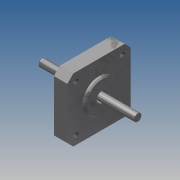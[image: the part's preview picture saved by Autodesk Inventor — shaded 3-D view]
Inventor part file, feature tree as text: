
AUTODESK INVENTOR PART (.ipt)
format: ipt  version: 2015 (Build 190159000, 159)  size: 141,824 bytes
history: native  units: mm
features: sketch x4, extrude x3, chamfer x3, hole x1, projected_geometry x1
ambient origin geometry x8: Origin, YZ Plane, XZ Plane, XY Plane, X Axis, Y Axis, Z Axis, Center Point
bodies: Body1 (feature_tree)
feature tree (12):
  extrude  "Extrusion2"  Depth=42.3mm
  hole  "Bohrung1"  [1 undecoded]
  extrude  "Extrusion3"  Depth=4.0mm
  chamfer  "Fase1"  Distance=4.0mm
  extrude  "Extrusion4"  Depth=2.0mm
  chamfer  "Fase2"  Distance=4.0mm
  chamfer  "Fase3"  Distance=7.0mm
  sketch  "Skizze1"  dims[d0=42.3mm d1=42.3mm]
  sketch  "Skizze2"  dims[d5=4.0mm d6=4.0mm]
  projected_geometry  "Projizierte Kontur1"
  sketch  "Skizze3"  dims[d7=4.0mm d8=4.0mm]
  sketch  "Skizze4"  dims[d9=4.0mm d10=4.0mm d11=4.0mm d12=4.0mm d13=7.0mm d16=9.0mm d17=0.0mm d18=15.5mm d19=15.5mm d20=3.242mm d21=5.0mm d22=4.0mm d23=2.0mm d24=90.0deg d25=11.8mm d26=20.594885mm d27=22.0mm d28=7.0mm d29=2.0mm d30=0.0mm d31=0.8mm d32=2.0mm d33=45.0deg d34=5.0mm d35=24.0mm d36=40.0mm d37=0.0mm d38=0.0mm d39=0.2mm d40=2.0mm d41=45.0deg d42=0.2mm d43=2.0mm d44=45.0deg]
note: 1 required parameter value undecoded (feature->parameter linkage not recoverable at this tier; creation-order binding heuristic only, values carry confidence <= 0.55)
